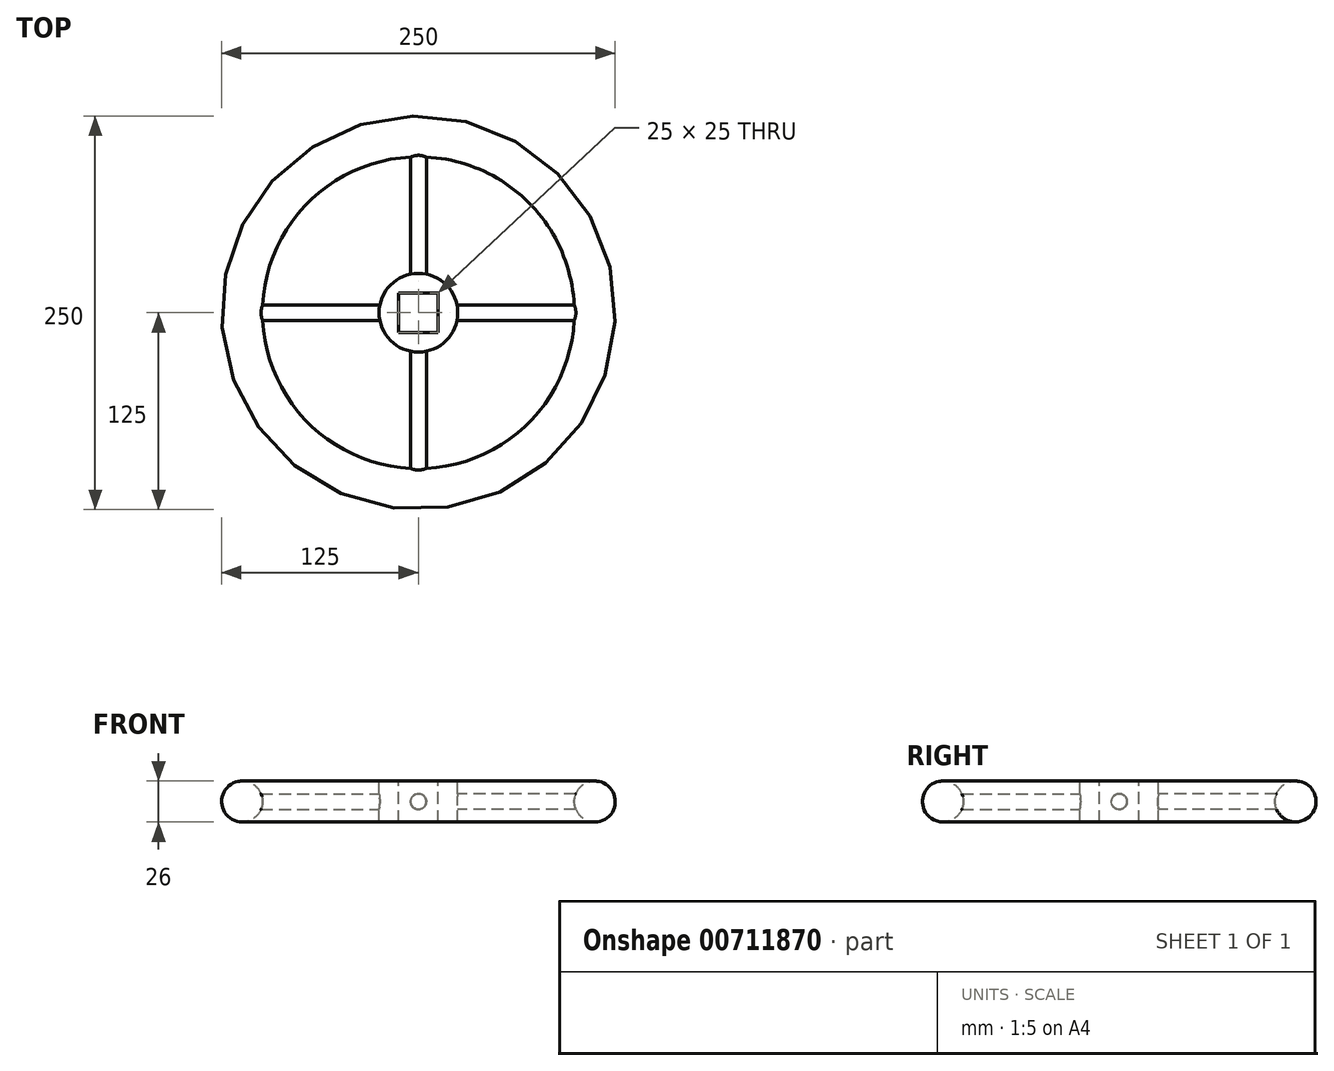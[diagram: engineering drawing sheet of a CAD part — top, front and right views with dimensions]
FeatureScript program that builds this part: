
annotation { "Feature Type Name" : "Feature", "Feature Type Description" : "" }
export const myFeature = defineFeature(function(context is Context, id is Id, definition is map)
    precondition{}
    {
        {
            var Q0;
            Q0=qCreatedBy(makeId("Front.planeOp"),FACE);
            var sketch = newSketch(context, id + "F0", { "sketchPlane" : qUnion([Q0])});
            skLineSegment(sketch, "E0", {"start": v(0, 30.64) * mm, "end": v(0, 0) * mm, "construction": true});
            skLineSegment(sketch, "E1", {"start": v(0, 0) * mm, "end": v(0, 13) * mm});
            skLineSegment(sketch, "E2", {"start": v(0, 0) * mm, "end": v(0, -13) * mm});
            skLineSegment(sketch, "E3", {"start": v(0, 13) * mm, "end": v(25, 13) * mm});
            skLineSegment(sketch, "E4", {"start": v(25, 13) * mm, "end": v(25, -13) * mm});
            skLineSegment(sketch, "E5", {"start": v(25, -13) * mm, "end": v(0, -13) * mm});
            skLineSegment(sketch, "E6", {"start": v(0, 0) * mm, "end": v(112, 0) * mm, "construction": true});
            skCircle(sketch, "E7", {"center": v(112, 0) * mm, "radius": 13 * mm});
            skSolve(sketch);
        }
        {
            var Q0;
            Q0 = qSketchRegion(id + "F0", true);
            var Q1;
            Q1=sQuery(id+"F0.wireOp",EDGE,"E0");
            revolve(context, id + "F1", {"surfaceOperationType" : NewSurfaceOperationType.NEW, "entities" : qUnion([Q0]), "axis" : qUnion([Q1]), "revolveType" : RevolveType.FULL});
        }
        {
            var Q0;
            Q0=makeQuery(id+"F1.opRevolve","SWEPT_FACE",FACE,{"disambiguationData":[OSD([sQuery(id+"F0.wireOp",EDGE,"E3")])]});
            var sketch = newSketch(context, id + "F2", { "sketchPlane" : qUnion([Q0])});
            skLineSegment(sketch, "E8.bottom", {"start": v(12.5, 12.5) * mm, "end": v(-12.5, 12.5) * mm});
            skLineSegment(sketch, "E8.top", {"start": v(12.5, -12.5) * mm, "end": v(-12.5, -12.5) * mm});
            skLineSegment(sketch, "E8.left", {"start": v(12.5, 12.5) * mm, "end": v(12.5, -12.5) * mm});
            skLineSegment(sketch, "E8.right", {"start": v(-12.5, 12.5) * mm, "end": v(-12.5, -12.5) * mm});
            skPoint(sketch, "E8.middle", {"position": v(0, 0) * mm});
            skSolve(sketch);
        }
        {
            var Q0;
            Q0 = qSketchRegion(id + "F2", true);
            extrude(context, id + "F3", {"entities" : qUnion([Q0]), "operationType" : NewBodyOperationType.REMOVE, "endBound" : BoundingType.THROUGH_ALL, "oppositeDirection" : true, "depth" : 25 * mm, "offsetDistance" : 25 * mm});
        }
        {
            var Q0;
            Q0=qCreatedBy(makeId("Top.planeOp"),FACE);
            var sketch = newSketch(context, id + "F4", { "sketchPlane" : qUnion([Q0])});
            skLineSegment(sketch, "E9", {"start": v(0, 0) * mm, "end": v(108.98, 0) * mm, "construction": true});
            skLineSegment(sketch, "E10.0", {"start": v(24.5, -5) * mm, "end": v(101.38, -5) * mm});
            skLineSegment(sketch, "E11", {"start": v(23.34, 0) * mm, "end": v(103.7, 0) * mm});
            skArc(sketch, "E12", {"start": v(24.5, -5) * mm, "mid": v(24.87, -2.51) * mm, "end": v(25, 0) * mm});
            skArc(sketch, "E13", {"start": v(101.38, -5) * mm, "mid": v(101.47, -2.5) * mm, "end": v(101.5, 0) * mm});
            skSolve(sketch);
        }
        {
            var Q0;
            Q0 = qSketchRegion(id + "F4", true);
            var Q1;
            Q1=sQuery(id+"F4.wireOp",EDGE,"E9");
            revolve(context, id + "F5", {"operationType" : NewBodyOperationType.ADD, "surfaceOperationType" : NewSurfaceOperationType.NEW, "entities" : qUnion([Q0]), "axis" : qUnion([Q1]), "revolveType" : RevolveType.FULL});
        }
        {
            var Q0;
            Q0=makeQuery(id+"F5.opRevolve","SWEPT_FACE",FACE,{"disambiguationData":[OSD([sQuery(id+"F4.wireOp",EDGE,"E10.0")])]});
            var Q1;
            Q1=makeQuery(id+"F1.opRevolve","SWEPT_EDGE",EDGE,{"disambiguationData":[OSD([sQuery(id+"F0.wireOp",EDGE,"E3"),sQuery(id+"F0.wireOp",EDGE,"E4")])]});
            circularPattern(context, id + "F6", {"patternType" : PatternType.FACE, "faces" : qUnion([Q0]), "axis" : qUnion([Q1]), "angle" : 360 * degree, "instanceCount" : 4, "equalSpace" : true});
        }
    });
